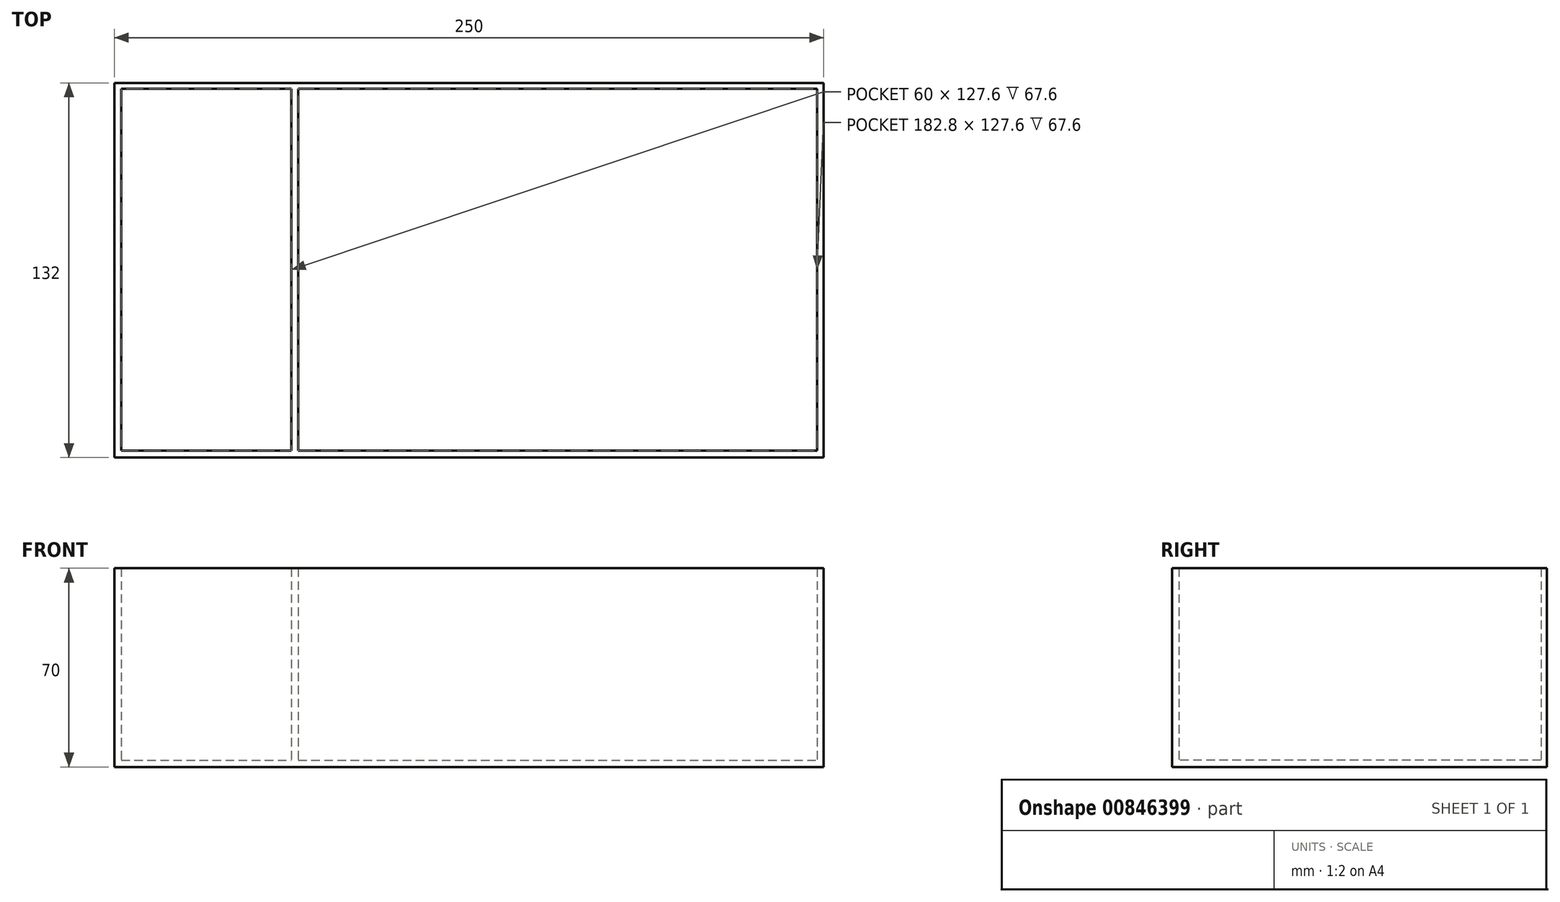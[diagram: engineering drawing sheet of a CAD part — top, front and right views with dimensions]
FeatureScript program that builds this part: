
annotation { "Feature Type Name" : "Feature", "Feature Type Description" : "" }
export const myFeature = defineFeature(function(context is Context, id is Id, definition is map)
    precondition{}
    {
        {
            var Q0;
            Q0=qCreatedBy(makeId("Top.planeOp"),FACE);
            var sketch = newSketch(context, id + "F0", { "sketchPlane" : qUnion([Q0])});
            skLineSegment(sketch, "E0.bottom", {"start": v(-125, 66) * mm, "end": v(125, 66) * mm});
            skLineSegment(sketch, "E0.top", {"start": v(-125, -66) * mm, "end": v(125, -66) * mm});
            skLineSegment(sketch, "E0.left", {"start": v(-125, 66) * mm, "end": v(-125, -66) * mm});
            skLineSegment(sketch, "E0.right", {"start": v(125, 66) * mm, "end": v(125, -66) * mm});
            skPoint(sketch, "E0.middle", {"position": v(0, 0) * mm});
            skLineSegment(sketch, "E1.0", {"start": v(-122.6, 63.6) * mm, "end": v(-122.6, -63.6) * mm});
            skLineSegment(sketch, "E1.1", {"start": v(-122.6, 64) * mm, "end": v(122.6, 64) * mm});
            skLineSegment(sketch, "E1.2", {"start": v(122.6, 63.6) * mm, "end": v(122.6, -63.6) * mm});
            skLineSegment(sketch, "E1.3", {"start": v(-122.6, -63.6) * mm, "end": v(122.6, -63.6) * mm});
            skLineSegment(sketch, "E2", {"start": v(-122.6, -63.6) * mm, "end": v(-62.6, -63.6) * mm});
            skLineSegment(sketch, "E3", {"start": v(-60.2, -63.6) * mm, "end": v(122.6, -63.6) * mm});
            skLineSegment(sketch, "E4.0", {"start": v(-62.6, 63.6) * mm, "end": v(-62.6, -63.6) * mm});
            skLineSegment(sketch, "E5.0", {"start": v(-60.2, 63.6) * mm, "end": v(-60.2, -63.6) * mm});
            skLineSegment(sketch, "E6", {"start": v(-62.6, 63.6) * mm, "end": v(-62.6, 64) * mm});
            skLineSegment(sketch, "E7", {"start": v(-60.2, 63.6) * mm, "end": v(-60.2, 64) * mm});
            skLineSegment(sketch, "E8", {"start": v(-122.6, 63.6) * mm, "end": v(-122.6, 64) * mm});
            skLineSegment(sketch, "E9", {"start": v(122.6, 63.6) * mm, "end": v(122.6, 64) * mm});
            skSolve(sketch);
        }
        {
            var Q0;
            Q0=makeQuery(id+"F0.imprint","IMPRINT",FACE,{"disambiguationData":[TD([[makeQuery(id+"F0.imprint","IMPRINT",EDGE,{"derivedFrom":sQuery(id+"F0.wireOp",EDGE,"E0.bottom")}),-1.0]])]});
            var Q1;
            {var subQ2=sQuery(id+"F0.wireOp",EDGE,"E4.0");Q1=makeQuery(id+"F0.imprint","IMPRINT",FACE,{"disambiguationData":[TD([[makeQuery(id+"F0.imprint","IMPRINT",EDGE,{"derivedFrom":subQ2}),1.0]])]});}
            extrude(context, id + "F1", {"entities" : qUnion([Q0, Q1]), "depth" : 70 * mm, "offsetDistance" : 25 * mm});
        }
        {
            var Q0;
            {var subQ2=sQuery(id+"F0.wireOp",EDGE,"E1.0");Q0=makeQuery(id+"F0.imprint","IMPRINT",FACE,{"disambiguationData":[TD([[makeQuery(id+"F0.imprint","IMPRINT",EDGE,{"derivedFrom":subQ2}),1.0]])]});}
            var Q1;
            {var subQ1=sQuery(id+"F0.wireOp",EDGE,"E1.2");Q1=makeQuery(id+"F0.imprint","IMPRINT",FACE,{"disambiguationData":[TD([[makeQuery(id+"F0.imprint","IMPRINT",EDGE,{"derivedFrom":subQ1}),-1.0]])]});}
            extrude(context, id + "F2", {"entities" : qUnion([Q0, Q1]), "operationType" : NewBodyOperationType.ADD, "depth" : 2.4 * mm, "offsetDistance" : 25 * mm});
        }
    });
